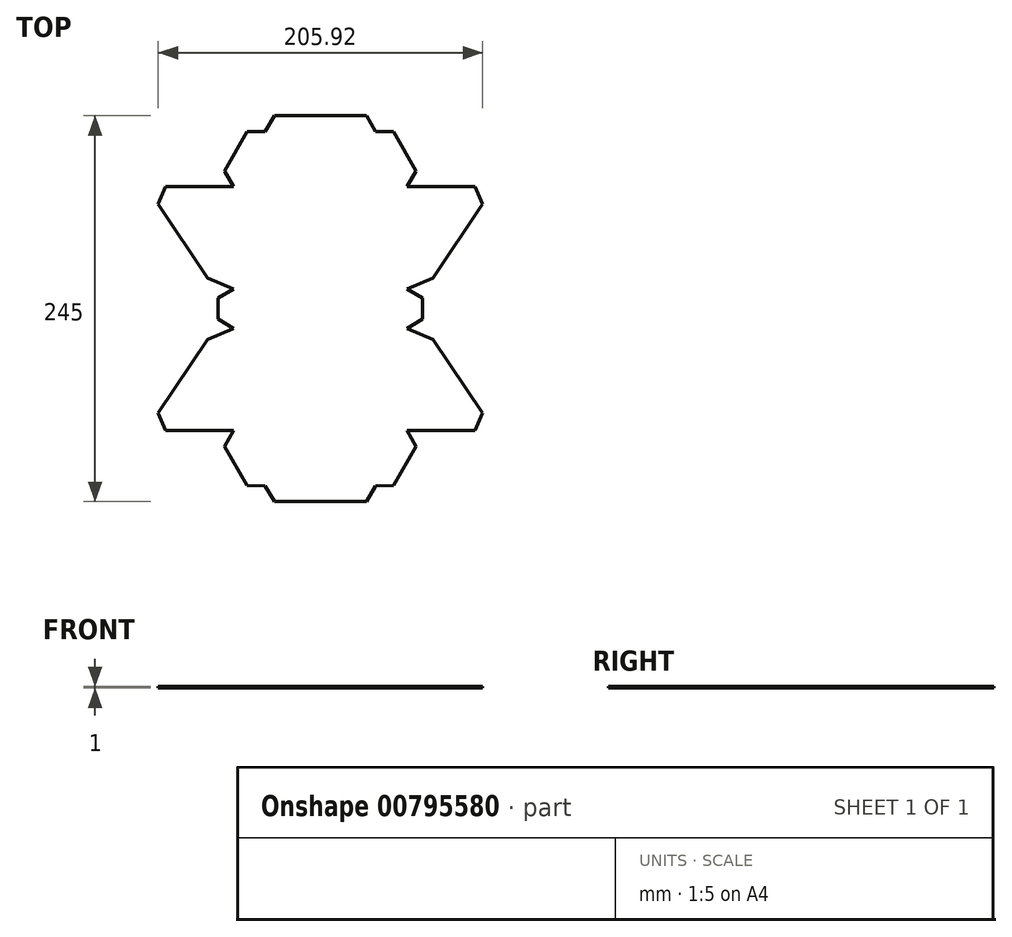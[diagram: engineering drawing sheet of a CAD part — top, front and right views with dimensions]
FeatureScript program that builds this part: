
annotation { "Feature Type Name" : "Feature", "Feature Type Description" : "" }
export const myFeature = defineFeature(function(context is Context, id is Id, definition is map)
    precondition{}
    {
        {
            var Q0;
            Q0=qCreatedBy(makeId("Top.planeOp"),FACE);
            var sketch = newSketch(context, id + "F0", { "sketchPlane" : qUnion([Q0])});
            skLineSegment(sketch, "E0.bottom", {"start": v(-55, 12.5) * mm, "end": v(55, 12.5) * mm, "construction": true});
            skLineSegment(sketch, "E0.top", {"start": v(-55, -12.5) * mm, "end": v(55, -12.5) * mm, "construction": true});
            skLineSegment(sketch, "E0.left", {"start": v(-55, 12.5) * mm, "end": v(-55, -12.5) * mm, "construction": true});
            skLineSegment(sketch, "E0.right", {"start": v(55, 12.5) * mm, "end": v(55, -12.5) * mm, "construction": true});
            skLineSegment(sketch, "E1.top", {"start": v(-55, -77.5) * mm, "end": v(55, -77.5) * mm, "construction": true});
            skLineSegment(sketch, "E1.left", {"start": v(-55, -12.5) * mm, "end": v(-55, -77.5) * mm, "construction": true});
            skLineSegment(sketch, "E1.right", {"start": v(55, -12.5) * mm, "end": v(55, -77.5) * mm, "construction": true});
            skLineSegment(sketch, "E2.MirrorCS", {"start": v(55, 12.5) * mm, "end": v(55, 77.5) * mm, "construction": true});
            skLineSegment(sketch, "E3.MirrorCS", {"start": v(-55, 12.5) * mm, "end": v(-55, 77.5) * mm, "construction": true});
            skLineSegment(sketch, "E4.MirrorCS", {"start": v(-55, 77.5) * mm, "end": v(55, 77.5) * mm, "construction": true});
            skLineSegment(sketch, "E5", {"start": v(-55, -77.5) * mm, "end": v(-35, -42.5) * mm, "construction": true});
            skLineSegment(sketch, "E6", {"start": v(-35, -42.5) * mm, "end": v(0, -42.5) * mm, "construction": true});
            skLineSegment(sketch, "E7", {"start": v(-35, -42.5) * mm, "end": v(-55, -12.5) * mm, "construction": true});
            skLineSegment(sketch, "E8.MirrorCS", {"start": v(-98.33, -77.5) * mm, "end": v(-55, -12.5) * mm, "construction": true});
            skLineSegment(sketch, "E9", {"start": v(-55, -77.5) * mm, "end": v(-98.33, -77.5) * mm});
            skPoint(sketch, "E10.orphan", {"position": v(-75, -42.5) * mm});
            skLineSegment(sketch, "E11.MirrorCS", {"start": v(-55, -77.5) * mm, "end": v(-35, -112.5) * mm, "construction": true});
            skLineSegment(sketch, "E12.MirrorCS", {"start": v(55, -77.5) * mm, "end": v(35, -112.5) * mm, "construction": true});
            skLineSegment(sketch, "E13", {"start": v(-35, -112.5) * mm, "end": v(35, -112.5) * mm, "construction": true});
            skLineSegment(sketch, "E14.MirrorCS", {"start": v(98.33, -77.5) * mm, "end": v(55, -12.5) * mm, "construction": true});
            skLineSegment(sketch, "E15.MirrorCS", {"start": v(55, -77.5) * mm, "end": v(98.33, -77.5) * mm});
            skLineSegment(sketch, "E16.MirrorCS", {"start": v(-98.33, 77.5) * mm, "end": v(-55, 12.5) * mm, "construction": true});
            skLineSegment(sketch, "E17.MirrorCS", {"start": v(-55, 77.5) * mm, "end": v(-98.33, 77.5) * mm});
            skLineSegment(sketch, "E18.MirrorCS", {"start": v(-55, 77.5) * mm, "end": v(-35, 112.5) * mm, "construction": true});
            skLineSegment(sketch, "E19.MirrorCS", {"start": v(55, 77.5) * mm, "end": v(35, 112.5) * mm, "construction": true});
            skLineSegment(sketch, "E20.MirrorCS", {"start": v(-35, 112.5) * mm, "end": v(35, 112.5) * mm, "construction": true});
            skLineSegment(sketch, "E21.MirrorCS", {"start": v(55, 77.5) * mm, "end": v(98.33, 77.5) * mm});
            skLineSegment(sketch, "E22.MirrorCS", {"start": v(98.33, 77.5) * mm, "end": v(55, 12.5) * mm, "construction": true});
            skPoint(sketch, "E23.orphan", {"position": v(-110.85, -172.27) * mm});
            skPoint(sketch, "E24.orphan", {"position": v(110.85, -172.27) * mm});
            skLineSegment(sketch, "E25.0", {"start": v(-86.31, -77.5) * mm, "end": v(-55, -30.53) * mm, "construction": true});
            skLineSegment(sketch, "E26.trimOffspring", {"start": v(-49, -21.51) * mm, "end": v(-46.86, -18.31) * mm});
            skLineSegment(sketch, "E27.0", {"start": v(43.48, -77.5) * mm, "end": v(29.2, -102.5) * mm, "construction": true});
            skLineSegment(sketch, "E27.1", {"start": v(-29.2, -102.5) * mm, "end": v(29.2, -102.5) * mm, "construction": true});
            skLineSegment(sketch, "E27.2", {"start": v(-43.48, -77.5) * mm, "end": v(-29.2, -102.5) * mm, "construction": true});
            skLineSegment(sketch, "E28.MirrorCS", {"start": v(-102.96, -66.4) * mm, "end": v(-71.64, -19.43) * mm});
            skLineSegment(sketch, "E29.MirrorCS", {"start": v(-60.85, -87.42) * mm, "end": v(-46.56, -112.42) * mm});
            skLineSegment(sketch, "E30.MirrorCS", {"start": v(-29.2, -122.5) * mm, "end": v(29.2, -122.5) * mm});
            skLineSegment(sketch, "E31.MirrorCS", {"start": v(60.85, -87.42) * mm, "end": v(46.56, -112.42) * mm});
            skPoint(sketch, "E32.MirrorP", {"position": v(29.5, -178) * mm});
            skLineSegment(sketch, "E33", {"start": v(-102.96, -66.4) * mm, "end": v(-98.33, -77.5) * mm});
            skLineSegment(sketch, "E34", {"start": v(-71.64, -19.43) * mm, "end": v(-55, -12.5) * mm});
            skLineSegment(sketch, "E35", {"start": v(-60.85, -87.42) * mm, "end": v(-55, -77.5) * mm});
            skLineSegment(sketch, "E36", {"start": v(-46.56, -112.42) * mm, "end": v(-35, -112.5) * mm});
            skLineSegment(sketch, "E37", {"start": v(-29.2, -122.5) * mm, "end": v(-35, -112.5) * mm});
            skLineSegment(sketch, "E38", {"start": v(29.2, -122.5) * mm, "end": v(35, -112.5) * mm});
            skLineSegment(sketch, "E39", {"start": v(46.56, -112.42) * mm, "end": v(35, -112.5) * mm});
            skLineSegment(sketch, "E40", {"start": v(60.85, -87.42) * mm, "end": v(55, -77.5) * mm});
            skLineSegment(sketch, "E41.MirrorCS", {"start": v(102.96, -66.4) * mm, "end": v(71.64, -19.43) * mm});
            skLineSegment(sketch, "E42.MirrorCS", {"start": v(102.96, -66.4) * mm, "end": v(98.33, -77.5) * mm});
            skLineSegment(sketch, "E43.MirrorCS", {"start": v(71.64, -19.43) * mm, "end": v(55, -12.5) * mm});
            skLineSegment(sketch, "E44.MirrorCS", {"start": v(-71.64, 19.43) * mm, "end": v(-55, 12.5) * mm});
            skLineSegment(sketch, "E45.MirrorCS", {"start": v(-102.96, 66.4) * mm, "end": v(-71.64, 19.43) * mm});
            skLineSegment(sketch, "E46.MirrorCS", {"start": v(-102.96, 66.4) * mm, "end": v(-98.33, 77.5) * mm});
            skLineSegment(sketch, "E47.MirrorCS", {"start": v(-60.85, 87.42) * mm, "end": v(-55, 77.5) * mm});
            skLineSegment(sketch, "E48.MirrorCS", {"start": v(-60.85, 87.42) * mm, "end": v(-46.56, 112.42) * mm});
            skLineSegment(sketch, "E49.MirrorCS", {"start": v(-46.56, 112.42) * mm, "end": v(-35, 112.5) * mm});
            skLineSegment(sketch, "E50.MirrorCS", {"start": v(-29.2, 122.5) * mm, "end": v(-35, 112.5) * mm});
            skLineSegment(sketch, "E51.MirrorCS", {"start": v(-29.2, 122.5) * mm, "end": v(29.2, 122.5) * mm});
            skLineSegment(sketch, "E52.MirrorCS", {"start": v(29.2, 122.5) * mm, "end": v(35, 112.5) * mm});
            skLineSegment(sketch, "E53.MirrorCS", {"start": v(46.56, 112.42) * mm, "end": v(35, 112.5) * mm});
            skLineSegment(sketch, "E54.MirrorCS", {"start": v(60.85, 87.42) * mm, "end": v(46.56, 112.42) * mm});
            skLineSegment(sketch, "E55.MirrorCS", {"start": v(60.85, 87.42) * mm, "end": v(55, 77.5) * mm});
            skLineSegment(sketch, "E56.MirrorCS", {"start": v(102.96, 66.4) * mm, "end": v(98.33, 77.5) * mm});
            skLineSegment(sketch, "E57.MirrorCS", {"start": v(102.96, 66.4) * mm, "end": v(71.64, 19.43) * mm});
            skLineSegment(sketch, "E58.MirrorCS", {"start": v(71.64, 19.43) * mm, "end": v(55, 12.5) * mm});
            skLineSegment(sketch, "E59.0", {"start": v(65, 6.73) * mm, "end": v(65, -6.73) * mm});
            skLineSegment(sketch, "E60", {"start": v(55, 12.5) * mm, "end": v(65, 6.73) * mm});
            skLineSegment(sketch, "E61.MirrorCS", {"start": v(55, -12.5) * mm, "end": v(65, -6.73) * mm});
            skLineSegment(sketch, "E62.MirrorCS", {"start": v(-55, 12.5) * mm, "end": v(-65, 6.73) * mm});
            skLineSegment(sketch, "E63.MirrorCS", {"start": v(-65, 6.73) * mm, "end": v(-65, -6.73) * mm});
            skLineSegment(sketch, "E64.MirrorCS", {"start": v(-55, -12.5) * mm, "end": v(-65, -6.73) * mm});
            skSolve(sketch);
        }
        {
            var Q0;
            Q0=makeQuery(id+"F0.imprint","IMPRINT",FACE,{"disambiguationData":[TD([[makeQuery(id+"F0.imprint","IMPRINT",EDGE,{"derivedFrom":sQuery(id+"F0.wireOp",EDGE,"E9")}),-1.0]])]});
            extrude(context, id + "F1", {"entities" : qUnion([Q0]), "depth" : 1 * mm, "offsetDistance" : 25 * mm});
        }
    });
